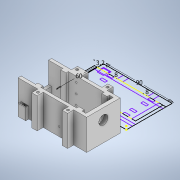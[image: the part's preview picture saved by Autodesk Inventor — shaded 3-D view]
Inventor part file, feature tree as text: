
AUTODESK INVENTOR PART (.ipt)
format: ipt  version: 2020.3 (Build 243373000, 373)  size: 561,664 bytes
history: native  units: mm
features: extrude x13, sketch x9, mirror x1
ambient origin geometry x8: Origin, YZ Plane, XZ Plane, XY Plane, X Axis, Y Axis, Z Axis, Center Point
bodies: Solid1 (feature_tree)
feature tree (23):
  sketch  "Sketch1"  dims[d0=90.0mm d1=60.0mm]
  extrude  "Extrusion1"  Depth=60.0mm
  extrude  "Extrusion2"  Depth=40.0mm TaperAngle=0.0deg
  extrude  "Extrusion3"  Depth=3.2mm
  extrude  "Extrusion4"  Depth=3.2mm
  sketch  "Sketch4"  dims[d9=3.2mm d10=3.2mm]
  extrude  "Extrusion5"  Depth=2.0mm
  extrude  "Extrusion6"  Depth=30.0mm
  extrude  "Extrusion7"  Depth=36.0mm TaperAngle=0.0deg
  extrude  "Extrusion8"  Depth=20.0mm TaperAngle=0.0deg
  extrude  "Extrusion9"  Depth=4.0mm TaperAngle=0.0deg
  sketch  "Sketch8"  dims[d18=36.0mm d19=0.0mm d20=36.0mm d21=0.0mm]
  extrude  "Extrusion14"  Depth=15.0mm TaperAngle=0.0deg
  extrude  "Extrusion15"  Depth=15.0mm TaperAngle=0.0deg
  extrude  "Extrusion16"  Depth=10.0mm
  mirror  "Mirror1"
  extrude  "Extrusion17"  Depth=10.0mm
  sketch  "Sketch2"  dims[d2=4.0mm d3=0.0mm d4=40.0mm d5=0.0mm]
  sketch  "Sketch3"  dims[d6=3.2mm d7=3.2mm]
  sketch  "Sketch5"  dims[d11=100.0mm d12=0.0mm d13=2.0mm]
  sketch  "Sketch6"  dims[d14=30.0mm d15=0.0mm d16=3.2mm]
  sketch  "Sketch9"  dims[d22=1.0mm d23=0.0mm d25=20.0mm d26=0.0mm]
  sketch  "Sketch10"  dims[d30=20.0mm d31=4.0mm d32=0.0mm d41=15.0mm d42=0.0mm d43=15.0mm d44=0.0mm d45=11.5mm d46=2.0mm d47=10.0mm d48=0.0mm d49=8.0mm d50=8.0mm d55=2.4mm d56=2.4mm d57=10.0mm d58=0.0mm]
